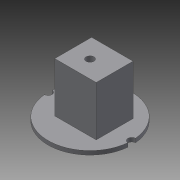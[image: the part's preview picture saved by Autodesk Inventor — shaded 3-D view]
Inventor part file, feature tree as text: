
AUTODESK INVENTOR PART (.ipt)
format: ipt  version: 2015 (Build 190159000, 159)  size: 105,472 bytes
history: native  units: mm
features: extrude x4, sketch x4, other x1
ambient origin geometry x8: Origin, YZ Plane, XZ Plane, XY Plane, X Axis, Y Axis, Z Axis, Center Point
bodies: Body1 (feature_tree)
feature tree (9):
  other  "ソリッド1"
  extrude  "押し出し1"  Depth=32.0mm
  extrude  "押し出し2"  Depth=1.5mm TaperAngle=0.0deg
  extrude  "押し出し3"  Depth=3.0mm
  extrude  "押し出し4"  Depth=3.0mm
  sketch  "スケッチ1"
  sketch  "スケッチ2"
  sketch  "スケッチ3"
  sketch  "スケッチ4"
